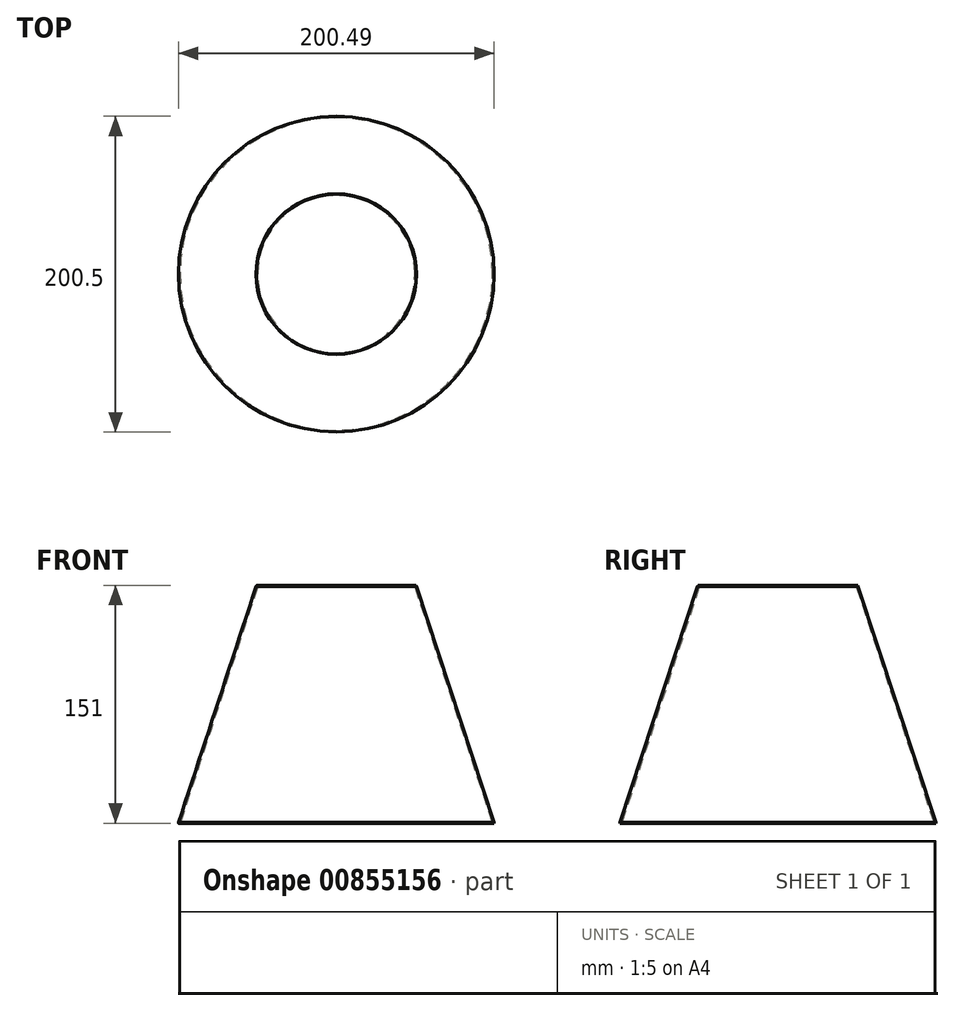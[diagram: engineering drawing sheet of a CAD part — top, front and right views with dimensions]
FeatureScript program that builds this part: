
annotation { "Feature Type Name" : "Feature", "Feature Type Description" : "" }
export const myFeature = defineFeature(function(context is Context, id is Id, definition is map)
    precondition{}
    {
        {
            var Q0;
            Q0=qCreatedBy(makeId("Front.planeOp"),FACE);
            var sketch = newSketch(context, id + "F0", { "sketchPlane" : qUnion([Q0])});
            skLineSegment(sketch, "E0", {"start": v(22.75, 36.17) * mm, "end": v(-27.25, 36.17) * mm});
            skLineSegment(sketch, "E1", {"start": v(-27.25, 36.17) * mm, "end": v(-76.54, -113.83) * mm});
            skLineSegment(sketch, "E2.0", {"start": v(-28.2, 36.48) * mm, "end": v(-77.5, -113.52) * mm});
            skLineSegment(sketch, "E3.0", {"start": v(22.75, 37.17) * mm, "end": v(-27.25, 37.17) * mm});
            skLineSegment(sketch, "E4", {"start": v(-28.2, 36.48) * mm, "end": v(-28, 37.17) * mm});
            skLineSegment(sketch, "E5", {"start": v(-28, 37.17) * mm, "end": v(-27.25, 37.17) * mm});
            skLineSegment(sketch, "E6", {"start": v(-76.54, -113.83) * mm, "end": v(-77.5, -113.83) * mm});
            skLineSegment(sketch, "E7", {"start": v(-77.5, -113.83) * mm, "end": v(-77.5, -113.52) * mm});
            skLineSegment(sketch, "E8", {"start": v(22.75, 37.17) * mm, "end": v(22.75, 36.17) * mm});
            skLineSegment(sketch, "E9", {"start": v(22.75, 36.17) * mm, "end": v(22.75, 112) * mm, "construction": true});
            skLineSegment(sketch, "E10", {"start": v(22.75, 112) * mm, "end": v(22.75, -109.2) * mm, "construction": true});
            skSolve(sketch);
        }
        {
            var Q0;
            Q0=makeQuery(id+"F0.imprint","IMPRINT",FACE,{"disambiguationData":[TD([[makeQuery(id+"F0.imprint","IMPRINT",EDGE,{"derivedFrom":sQuery(id+"F0.wireOp",EDGE,"E0")}),-1.0]])]});
            var Q1;
            Q1=sQuery(id+"F0.wireOp",EDGE,"E10");
            revolve(context, id + "F1", {"surfaceOperationType" : NewSurfaceOperationType.NEW, "entities" : qUnion([Q0]), "axis" : qUnion([Q1]), "revolveType" : RevolveType.SYMMETRIC, "oppositeDirection" : true, "angle" : 360 * degree});
        }
        {
            var Q0;
            Q0=makeQuery(id+"F1.opRevolve","SWEPT_FACE",FACE,{"disambiguationData":[OSD([sQuery(id+"F0.wireOp",EDGE,"E2.0")])]});
            chamfer(context, id + "F2", {"entities" : qUnion([Q0]), "width" : 0.5 * mm, "tangentPropagation" : true});
        }
    });
